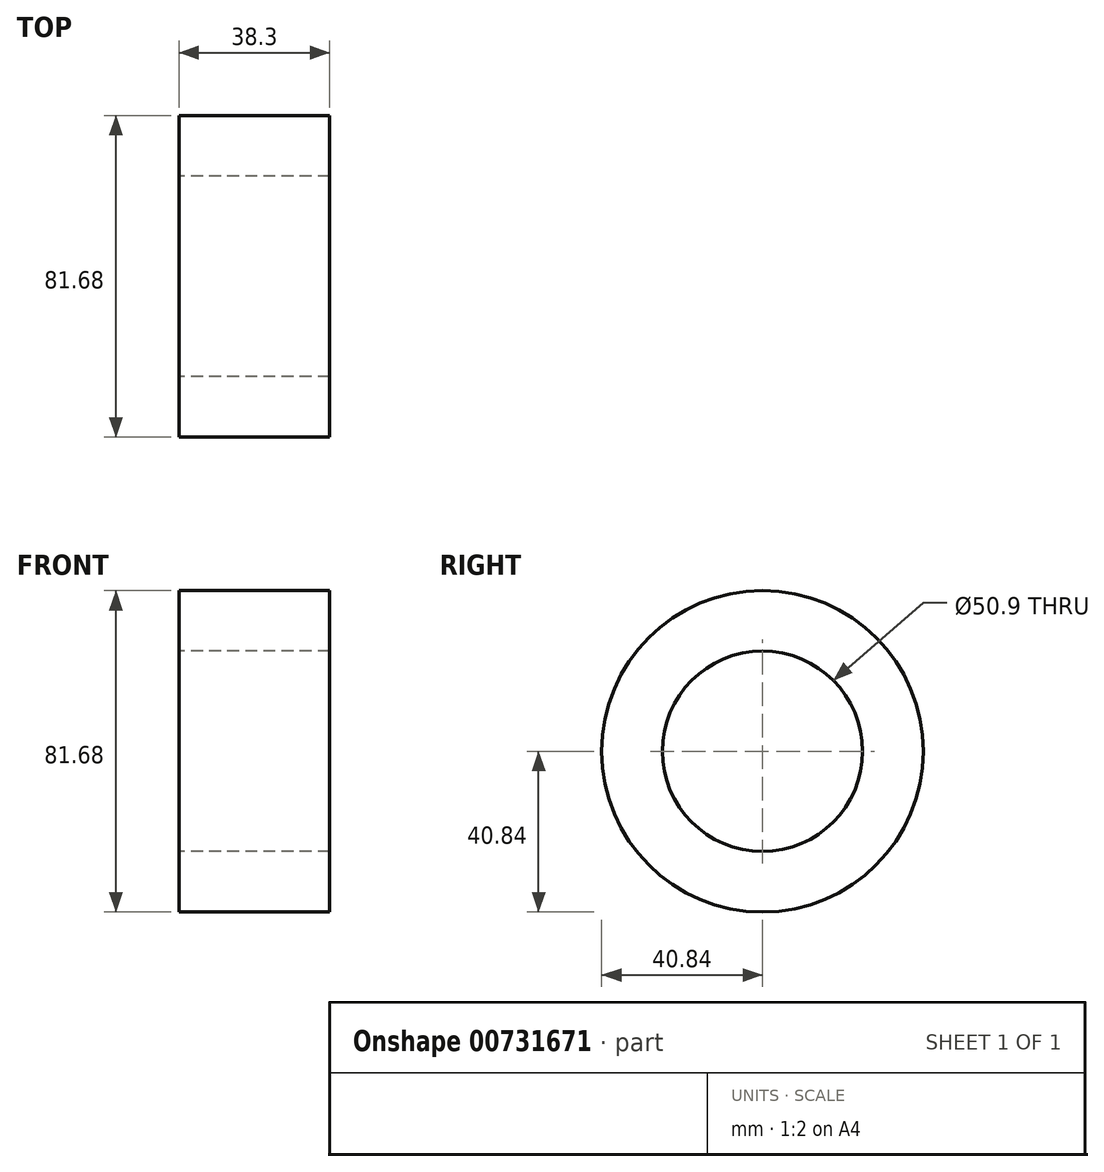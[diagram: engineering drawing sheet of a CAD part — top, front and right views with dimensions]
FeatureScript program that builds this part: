
annotation { "Feature Type Name" : "Feature", "Feature Type Description" : "" }
export const myFeature = defineFeature(function(context is Context, id is Id, definition is map)
    precondition{}
    {
        {
            var Q0;
            Q0=qCreatedBy(makeId("Front.planeOp"),FACE);
            var sketch = newSketch(context, id + "F0", { "sketchPlane" : qUnion([Q0])});
            skLineSegment(sketch, "E0", {"start": v(-35.34, 0) * mm, "end": v(54.67, 0) * mm});
            skLineSegment(sketch, "E1.bottom", {"start": v(-13.15, 40.84) * mm, "end": v(25.15, 40.84) * mm});
            skLineSegment(sketch, "E1.top", {"start": v(-13.15, 25.45) * mm, "end": v(25.15, 25.45) * mm});
            skLineSegment(sketch, "E1.left", {"start": v(-13.15, 40.84) * mm, "end": v(-13.15, 25.45) * mm});
            skLineSegment(sketch, "E1.right", {"start": v(25.15, 40.84) * mm, "end": v(25.15, 25.45) * mm});
            skSolve(sketch);
        }
        {
            var Q0;
            Q0=makeQuery(id+"F0.imprint","IMPRINT",FACE,{"disambiguationData":[TD([[makeQuery(id+"F0.imprint","IMPRINT",EDGE,{"derivedFrom":sQuery(id+"F0.wireOp",EDGE,"E1.bottom")}),-1.0]])]});
            var Q1;
            Q1=sQuery(id+"F0.wireOp",EDGE,"E0");
            revolve(context, id + "F1", {"surfaceOperationType" : NewSurfaceOperationType.NEW, "entities" : qUnion([Q0]), "axis" : qUnion([Q1]), "revolveType" : RevolveType.FULL});
        }
    });
